# Revit family: Furniture-Console_Table_Legs-KALLISTA-One-P46010-1
name_source: partatom
category: Specialty Equipment
units: mm (PartAtom-declared; Revit-internal decimal feet)

## family parameters
Cut with Voids When Loaded = No
Host = Face
Maintain Annotation Orientation = No
OmniClass Number = 23.21.19.15
Part Type = Normal
Room Calculation Point = No
Round Connector Dimension = Use Diameter
Shared = No

## types (6) — shared parameters
ADA Compliant = No
Assembly Code = E20
Date Modified = 05/22/2025
Default Elevation = 48"
Description = Console Table Legs
Height = 35"
Length = 21 3/8"
Manufacturer = Kallista Co.
Master Format 2014 = 06 41 93
Master Format 2014 Name = Cabinet and Drawer Hardware
Material = Primium Metal Construction
Product Documentation Link = https://techcomm.kohler.com
Product Name = One
URL = https://www.kallista.com
WaterSense Certified = No
Width = 25 11/16"

## per-type parameters (varying)
| type | Finish | Model | Product Page URL | Type |
| BL-Matte Black | Kallista-Metal-BL-Matte_Black | P46010-00-BL | https://www.kallista.com | 1 |
| BN-Brushed Nickel | Kallista-Metal-BN-Brushed_Nickel | P46010-00-BN |  | 2 |
| CP-Chrome | Kallista-Metal-CP-Chrome | P46010-00-CP |  | 3 |
| SN-Polished Nickel | Kallista-Metal-SN-Polished_Nickel | P46010-00-SN |  | 4 |
| ULB-Unlaquered Brass | Kallista-Metal-ULB-Unlaquered_Brass | P46010-00-ULB |  | 5 |
| BV-Brushed Bronze | Kallista-Metal-BV-Brushed_Bronze | P46010-00-BV |  | 6 |

## geometry (parser evidence)
native form markers: Sweep x4
no freeform markers — native parametric forms only
